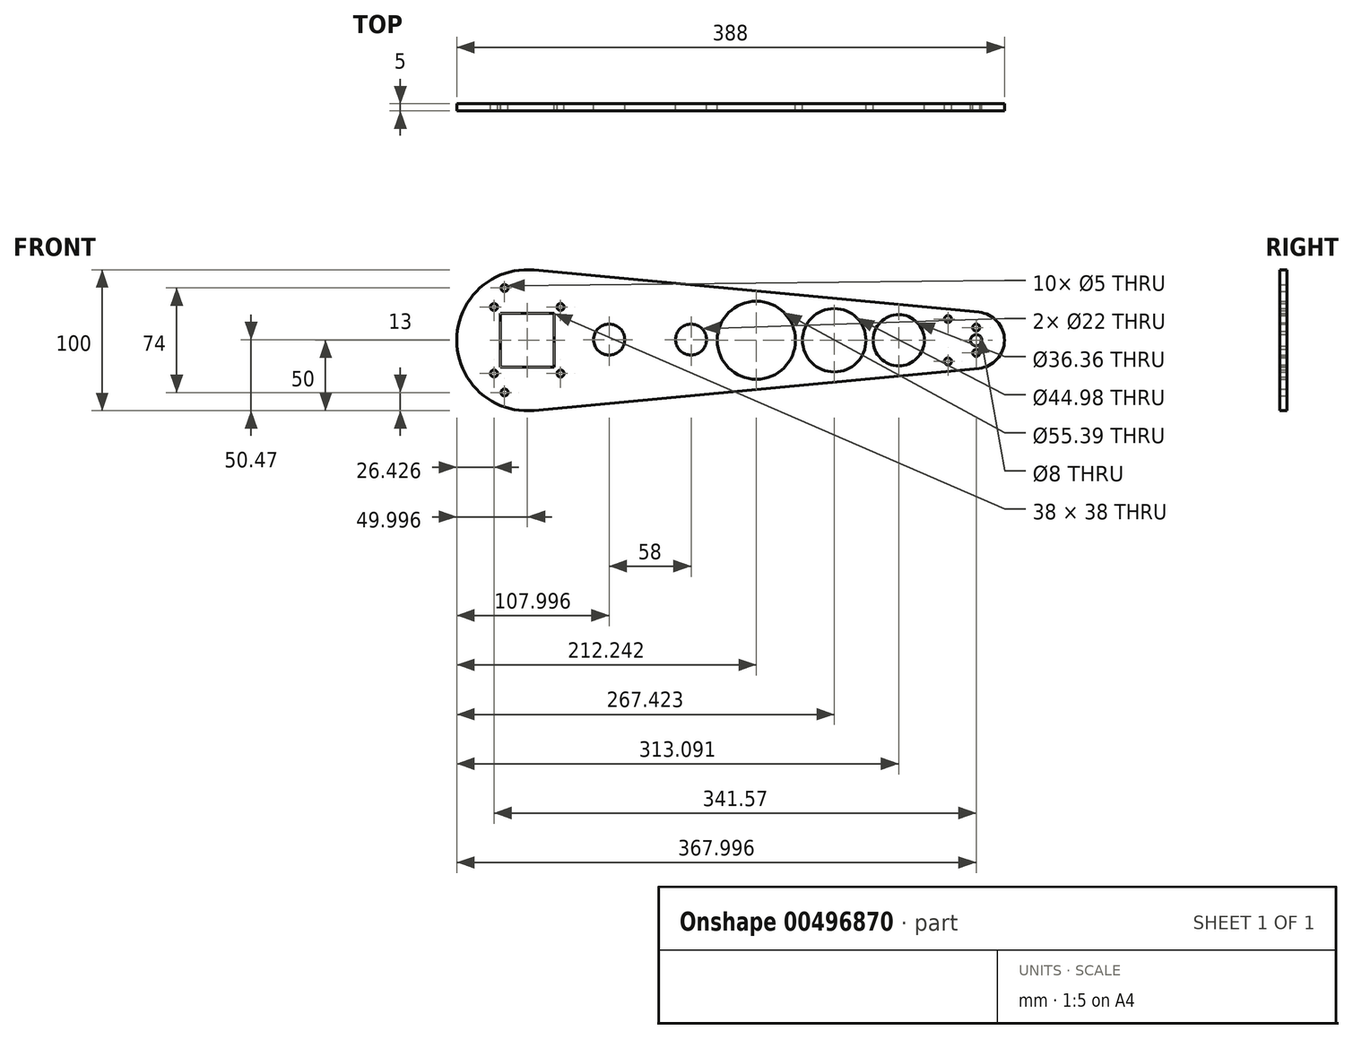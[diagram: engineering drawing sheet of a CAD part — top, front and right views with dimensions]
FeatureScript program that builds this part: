
annotation { "Feature Type Name" : "Feature", "Feature Type Description" : "" }
export const myFeature = defineFeature(function(context is Context, id is Id, definition is map)
    precondition{}
    {
        {
            var Q0;
            Q0=qCreatedBy(makeId("Front.planeOp"),FACE);
            var sketch = newSketch(context, id + "F0", { "sketchPlane" : qUnion([Q0])});
            skArc(sketch, "E0", {"start": v(-121.74, 49.78) * mm, "mid": v(-176.45, 0) * mm, "end": v(-121.74, -49.78) * mm});
            skCircle(sketch, "E1", {"center": v(-68.45, 0.47) * mm, "radius": 11 * mm});
            skCircle(sketch, "E2", {"center": v(-10.45, 0.47) * mm, "radius": 11 * mm});
            skCircle(sketch, "E3", {"center": v(-150.02, 23.57) * mm, "radius": 2.5 * mm});
            skCircle(sketch, "E4", {"center": v(-102.88, 23.57) * mm, "radius": 2.5 * mm});
            skCircle(sketch, "E5", {"center": v(-102.88, -23.57) * mm, "radius": 2.5 * mm});
            skCircle(sketch, "E6", {"center": v(-150.02, -23.57) * mm, "radius": 2.5 * mm});
            skCircle(sketch, "E7", {"center": v(191.55, 0) * mm, "radius": 4 * mm});
            skArc(sketch, "E8", {"start": v(193.43, -19.91) * mm, "mid": v(211.55, 0) * mm, "end": v(193.43, 19.91) * mm});
            skLineSegment(sketch, "E9", {"start": v(-121.74, 49.78) * mm, "end": v(193.43, 19.91) * mm});
            skLineSegment(sketch, "E10", {"start": v(-121.74, -49.78) * mm, "end": v(193.43, -19.91) * mm});
            skCircle(sketch, "E11", {"center": v(-142.58, 37) * mm, "radius": 2.5 * mm});
            skCircle(sketch, "E12", {"center": v(-142.58, -37) * mm, "radius": 2.5 * mm});
            skCircle(sketch, "E13", {"center": v(171.55, 15) * mm, "radius": 2.5 * mm});
            skCircle(sketch, "E14", {"center": v(171.55, -15) * mm, "radius": 2.5 * mm});
            skLineSegment(sketch, "E15", {"start": v(191.55, 0) * mm, "end": v(191.55, 9) * mm});
            skLineSegment(sketch, "E16", {"start": v(191.55, 0) * mm, "end": v(191.55, -9) * mm});
            skCircle(sketch, "E17", {"center": v(191.55, 9) * mm, "radius": 2.5 * mm});
            skCircle(sketch, "E18", {"center": v(191.55, -9) * mm, "radius": 2.5 * mm});
            skCircle(sketch, "E19", {"center": v(35.8, 0) * mm, "radius": 27.7 * mm});
            skCircle(sketch, "E20", {"center": v(90.97, 0) * mm, "radius": 22.49 * mm});
            skCircle(sketch, "E21", {"center": v(136.64, 0) * mm, "radius": 18.18 * mm});
            skLineSegment(sketch, "E22.bottom", {"start": v(-107.45, 19) * mm, "end": v(-145.45, 19) * mm});
            skLineSegment(sketch, "E22.top", {"start": v(-107.45, -19) * mm, "end": v(-145.45, -19) * mm});
            skLineSegment(sketch, "E22.left", {"start": v(-107.45, 19) * mm, "end": v(-107.45, -19) * mm});
            skLineSegment(sketch, "E22.right", {"start": v(-145.45, 19) * mm, "end": v(-145.45, -19) * mm});
            skSolve(sketch);
        }
        {
            var Q0;
            Q0=qSketchRegion(id+"F0",true);
            extrude(context, id + "F1", {"entities" : qUnion([Q0]), "depth" : 5 * mm});
        }
    });
